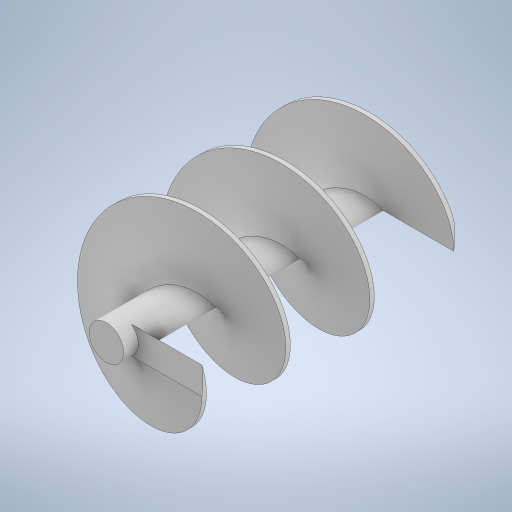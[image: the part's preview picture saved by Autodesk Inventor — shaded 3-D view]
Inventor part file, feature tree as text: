
AUTODESK INVENTOR PART (.ipt)
format: ipt  version: 2023 (Build 270158000, 158)  size: 1,356,800 bytes
history: native  units: in
note: dims shown in document units (in); Inventor stores cm internally (conversion verified against a paired STEP export)
features: sketch x4, extrude x4, other x2, sweep x1
ambient origin geometry x8: Origin, YZ Plane, XZ Plane, XY Plane, X Axis, Y Axis, Z Axis, Center Point
bodies: Solid1 (feature_tree)
feature tree (11):
  sketch  "Sketch1"  dims[d0=1.7717in d1=0.374in]
  extrude  "Extrusion1"  Depth=0.374in
  sketch  "Sketch2"  dims[d2=2.7165in d3=0.0in d4=2.7165in d5=1.1811in d6=0.5906in d7=0.0in]
  other  "Work Axis1"
  sweep  "Sweep1"
  extrude  "Extrusion3"  Depth=0.0984in
  extrude  "Extrusion4"  Depth=0.0984in
  extrude  "Extrusion5"  Depth=0.3543in TaperAngle=0.0deg
  sketch  "Sketch3"  dims[d10=0.0in d11=0.0in d12=0.0984in d13=0.0984in d14=0.5906in d15=0.0in d18=0.1575in d19=0.0in d20=0.3543in d21=0.0in]
  sketch  "3D Sketch1"
  other  "Helical Curve1"
